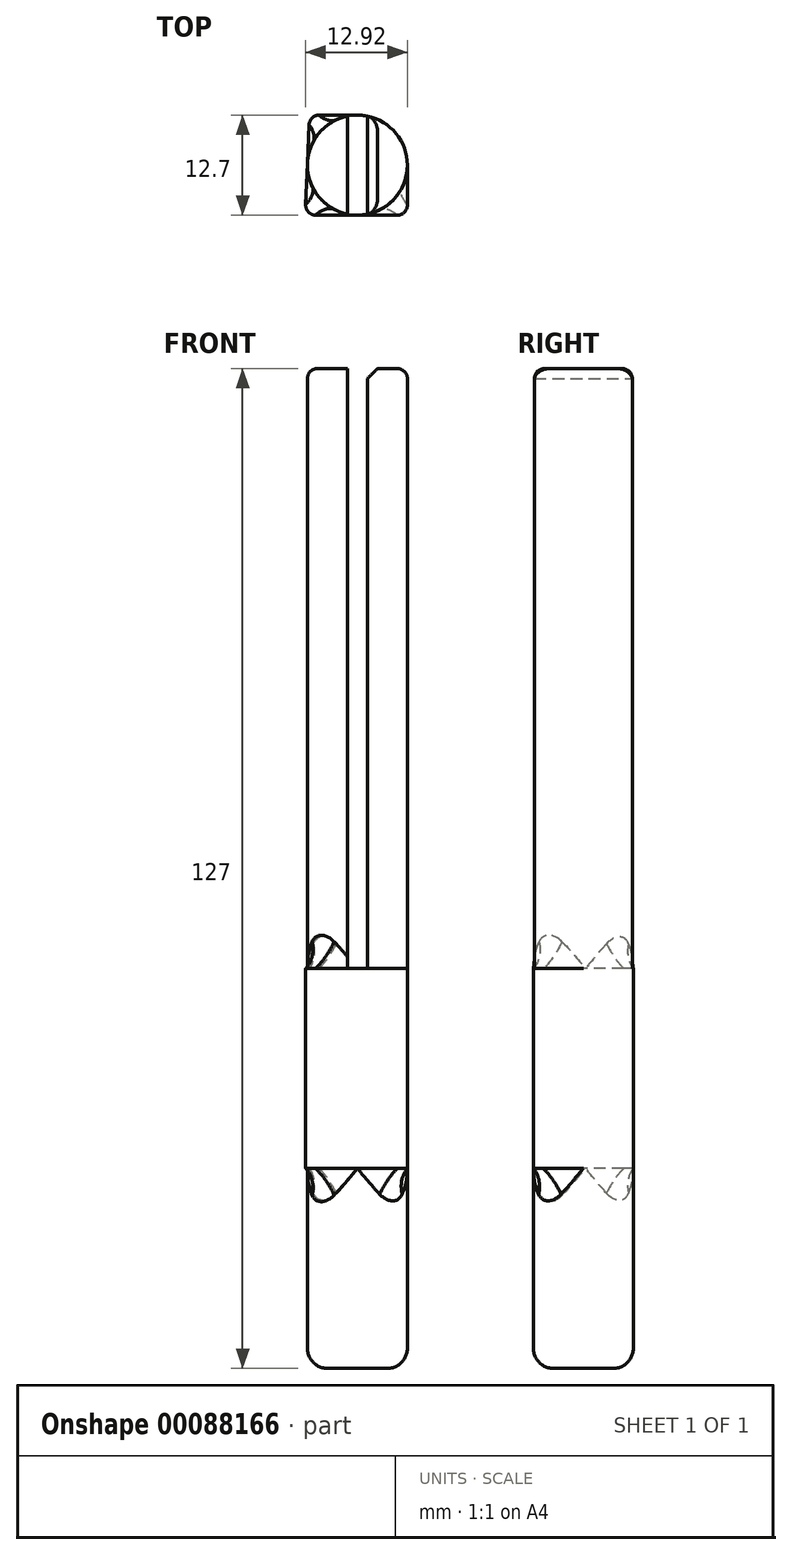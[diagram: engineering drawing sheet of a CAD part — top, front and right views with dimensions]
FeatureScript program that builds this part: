
annotation { "Feature Type Name" : "Feature", "Feature Type Description" : "" }
export const myFeature = defineFeature(function(context is Context, id is Id, definition is map)
    precondition{}
    {
        {
            var Q0;
            Q0=qCreatedBy(makeId("Top.planeOp"),FACE);
            var sketch = newSketch(context, id + "F0", { "sketchPlane" : qUnion([Q0])});
            skCircle(sketch, "E0", {"center": v(0, 0) * mm, "radius": 6.35 * mm});
            skSolve(sketch);
        }
        {
            var Q0;
            Q0=makeQuery(id+"F0.imprint","IMPRINT",FACE,{"disambiguationData":[TD([[makeQuery(id+"F0.imprint","IMPRINT",EDGE,{"derivedFrom":sQuery(id+"F0.wireOp",EDGE,"E0")}),1.0]])]});
            extrude(context, id + "F1", {"entities" : qUnion([Q0]), "depth" : 25.4 * mm});
        }
        {
            var Q0;
            Q0=makeQuery(id+"F1.opExtrude","CAP_FACE",FACE,{"disambiguationData":[OSD([sQuery(id+"F0.wireOp",EDGE,"E0")])],"isStart":false});
            var sketch = newSketch(context, id + "F2", { "sketchPlane" : qUnion([Q0])});
            skLineSegment(sketch, "E1.left", {"start": v(6.35, -6.35) * mm, "end": v(6.35, 6.35) * mm});
            skPoint(sketch, "E1.middle", {"position": v(0, 0) * mm});
            skCircle(sketch, "E2.cCircle", {"center": v(0, 0) * mm, "radius": 6.35 * mm, "construction": true});
            skLineSegment(sketch, "E2.0", {"start": v(6.35, 6.35) * mm, "end": v(6.35, -6.35) * mm});
            skLineSegment(sketch, "E2.1", {"start": v(6.35, -6.35) * mm, "end": v(-6.63, -6.35) * mm});
            skLineSegment(sketch, "E2.2", {"start": v(-6.08, 6.35) * mm, "end": v(6.35, 6.35) * mm});
            skPoint(sketch, "E2.0.midPoint", {"position": v(6.35, 0) * mm});
            skLineSegment(sketch, "E3", {"start": v(-6.08, 6.35) * mm, "end": v(-6.63, -6.35) * mm});
            skSolve(sketch);
        }
        {
            var Q0;
            {var subQ0=sQuery(id+"F2.wireOp",EDGE,"E2.2");var subQ1=sQuery(id+"F2.wireOp",EDGE,"E2.1");var subQ2=makeQuery(id+"F2.imprint","INTERSECT",VERTEX,{"derivedFrom":[subQ1,subQ0]});Q0=makeQuery(id+"F2.imprint","IMPRINT",FACE,{"disambiguationData":[TD([[makeQuery(id+"F2.imprint","IMPRINT",EDGE,{"disambiguationData":[TD([[subQ2,1.0]])],"derivedFrom":subQ1}),-1.0]])]});}
            var Q1;
            {var subQ0=makeQuery(id+"F1.opExtrude","CAP_EDGE",EDGE,{"disambiguationData":[OSD([sQuery(id+"F0.wireOp",EDGE,"E0")])],"isStart":false});var subQ1=makeQuery(id+"F2.imprint","INTERSECT",VERTEX,{"derivedFrom":[subQ0,sQuery(id+"F2.wireOp",EDGE,"E2.0")]});Q1=makeQuery(id+"F2.imprint","IMPRINT",FACE,{"disambiguationData":[TD([[makeQuery(id+"F2.imprint","IMPRINT",EDGE,{"disambiguationData":[TD([[subQ1,1.0]])],"derivedFrom":subQ0}),1.0]])]});}
            var Q2;
            {var subQ0=sQuery(id+"F2.wireOp",EDGE,"E2.2");var subQ1=sQuery(id+"F2.wireOp",EDGE,"E2.0");var subQ2=makeQuery(id+"F2.imprint","INTERSECT",VERTEX,{"derivedFrom":[subQ1,subQ0]});Q2=makeQuery(id+"F2.imprint","IMPRINT",FACE,{"disambiguationData":[TD([[makeQuery(id+"F2.imprint","IMPRINT",EDGE,{"disambiguationData":[TD([[subQ2,-1.0]])],"derivedFrom":subQ1}),-1.0]])]});}
            var Q3;
            {var subQ0=sQuery(id+"F2.wireOp",EDGE,"E2.1");var subQ1=sQuery(id+"F2.wireOp",EDGE,"E2.0");var subQ2=makeQuery(id+"F2.imprint","INTERSECT",VERTEX,{"derivedFrom":[subQ1,subQ0]});Q3=makeQuery(id+"F2.imprint","IMPRINT",FACE,{"disambiguationData":[TD([[makeQuery(id+"F2.imprint","IMPRINT",EDGE,{"disambiguationData":[TD([[subQ2,1.0]])],"derivedFrom":subQ1}),-1.0]])]});}
            var Q4;
            {var subQ0=sQuery(id+"F2.wireOp",EDGE,"E3");var subQ1=sQuery(id+"F2.wireOp",EDGE,"E2.2");var subQ2=makeQuery(id+"F2.imprint","INTERSECT",VERTEX,{"derivedFrom":[subQ1,subQ0]});Q4=makeQuery(id+"F2.imprint","IMPRINT",FACE,{"disambiguationData":[TD([[makeQuery(id+"F2.imprint","IMPRINT",EDGE,{"disambiguationData":[TD([[subQ2,-1.0]])],"derivedFrom":subQ1}),-1.0]])]});}
            extrude(context, id + "F3", {"entities" : qUnion([Q0, Q1, Q2, Q3, Q4]), "operationType" : NewBodyOperationType.ADD, "depth" : 25.4 * mm, "offsetDistance" : 25.4 * mm});
        }
        {
            var Q0;
            Q0=makeQuery(id+"F3.opExtrude","CAP_FACE",FACE,{"disambiguationData":[OSD([sQuery(id+"F2.wireOp",EDGE,"E2.0"),sQuery(id+"F2.wireOp",EDGE,"E2.1"),sQuery(id+"F2.wireOp",EDGE,"E2.2")])],"isStart":false});
            var sketch = newSketch(context, id + "F4", { "sketchPlane" : qUnion([Q0])});
            skCircle(sketch, "E4", {"center": v(0, 0) * mm, "radius": 6.35 * mm});
            skSolve(sketch);
        }
        {
            var Q0;
            {var subQ0=sQuery(id+"F4.wireOp",EDGE,"E4");var subQ1=makeQuery(id+"F4.imprint","INTERSECT",VERTEX,{"derivedFrom":[makeQuery(id+"F3.opExtrude","CAP_EDGE",EDGE,{"disambiguationData":[OSD([sQuery(id+"F2.wireOp",EDGE,"E1.top")])],"isStart":false}),subQ0]});Q0=makeQuery(id+"F4.imprint","IMPRINT",FACE,{"disambiguationData":[TD([[makeQuery(id+"F4.imprint","IMPRINT",EDGE,{"disambiguationData":[TD([[subQ1,1.0]])],"derivedFrom":subQ0}),1.0]])]});}
            extrude(context, id + "F5", {"entities" : qUnion([Q0]), "operationType" : NewBodyOperationType.ADD, "depth" : 76.2 * mm});
        }
        {
            var Q0;
            Q0=makeQuery(id+"F5.opExtrude","CAP_FACE",FACE,{"disambiguationData":[OSD([sQuery(id+"F4.wireOp",EDGE,"E4")])],"isStart":false});
            var sketch = newSketch(context, id + "F6", { "sketchPlane" : qUnion([Q0])});
            skLineSegment(sketch, "E5.bottom", {"start": v(1.27, 6.35) * mm, "end": v(-1.27, 6.35) * mm});
            skLineSegment(sketch, "E5.top", {"start": v(1.27, -6.35) * mm, "end": v(-1.27, -6.35) * mm});
            skLineSegment(sketch, "E5.left", {"start": v(1.27, 6.35) * mm, "end": v(1.27, -6.35) * mm});
            skLineSegment(sketch, "E5.right", {"start": v(-1.27, 6.35) * mm, "end": v(-1.27, -6.35) * mm});
            skPoint(sketch, "E5.middle", {"position": v(0, 0) * mm});
            skSolve(sketch);
        }
        {
            var Q0;
            {var subQ0=makeQuery(id+"F5.opExtrude","CAP_EDGE",EDGE,{"disambiguationData":[OSD([sQuery(id+"F4.wireOp",EDGE,"E4")])],"isStart":false});var subQ5=sQuery(id+"F6.wireOp",EDGE,"E5.left");var subQ6=makeQuery(id+"F6.imprint","INTERSECT",VERTEX,{"disambiguationData":[OD(0.0)],"derivedFrom":[subQ0,subQ5]});Q0=makeQuery(id+"F6.imprint","IMPRINT",FACE,{"disambiguationData":[TD([[makeQuery(id+"F6.imprint","IMPRINT",EDGE,{"disambiguationData":[TD([[subQ6,-1.0]])],"derivedFrom":subQ5}),-1.0]])]});}
            extrude(context, id + "F7", {"entities" : qUnion([Q0]), "operationType" : NewBodyOperationType.REMOVE, "oppositeDirection" : true, "depth" : 76.2 * mm});
        }
        {
            var Q0;
            Q0=makeQuery(id+"F7.boolean.opBoolean","COPY",EDGE,{"derivedFrom":makeQuery(id+"F7.opExtrude","CAP_EDGE",EDGE,{"disambiguationData":[OSD([sQuery(id+"F6.wireOp",EDGE,"E5.right")])],"isStart":true})});
            var Q1;
            Q1=makeQuery(id+"F7.boolean.opBoolean","COPY",EDGE,{"derivedFrom":makeQuery(id+"F7.opExtrude","CAP_EDGE",EDGE,{"disambiguationData":[OSD([sQuery(id+"F6.wireOp",EDGE,"E5.left")])],"isStart":true})});
            chamfer(context, id + "F8", {"entities" : qUnion([Q0, Q1]), "width" : 1.27 * mm, "tangentPropagation" : true});
        }
        {
            var Q0;
            {var subQ0=sQuery(id+"F4.wireOp",EDGE,"E4");Q0=makeQuery(id+"F7.boolean.opBoolean","SPLIT",EDGE,{"disambiguationData":[TD([makeQuery(id+"F7.opExtrude","SWEPT_FACE",FACE,{"disambiguationData":[OSD([sQuery(id+"F6.wireOp",EDGE,"E5.left")])]})])],"derivedFrom":makeQuery(id+"F5.opExtrude","CAP_EDGE",EDGE,{"disambiguationData":[OSD([subQ0])],"isStart":false})});}
            var Q1;
            {var subQ0=sQuery(id+"F4.wireOp",EDGE,"E4");Q1=makeQuery(id+"F7.boolean.opBoolean","SPLIT",EDGE,{"disambiguationData":[TD([makeQuery(id+"F7.opExtrude","SWEPT_FACE",FACE,{"disambiguationData":[OSD([sQuery(id+"F6.wireOp",EDGE,"E5.right")])]})])],"derivedFrom":makeQuery(id+"F5.opExtrude","CAP_EDGE",EDGE,{"disambiguationData":[OSD([subQ0])],"isStart":false})});}
            fillet(context, id + "F9", {"entities" : qUnion([Q0, Q1]), "radius" : 1.27 * mm, "tangentPropagation" : true, "allowEdgeOverflow" : false});
        }
        {
            var Q0;
            Q0=makeQuery(id+"F3.opExtrude","SWEPT_EDGE",EDGE,{"disambiguationData":[OSD([sQuery(id+"F2.wireOp",EDGE,"E2.0"),sQuery(id+"F2.wireOp",EDGE,"E2.2")])]});
            var Q1;
            Q1=makeQuery(id+"F3.opExtrude","SWEPT_EDGE",EDGE,{"disambiguationData":[OSD([sQuery(id+"F2.wireOp",EDGE,"E2.0"),sQuery(id+"F2.wireOp",EDGE,"E2.1")])]});
            var Q2;
            Q2=makeQuery(id+"F3.opExtrude","SWEPT_EDGE",EDGE,{"disambiguationData":[OSD([sQuery(id+"F2.wireOp",EDGE,"E2.1"),sQuery(id+"F2.wireOp",EDGE,"E2.2")])]});
            fillet(context, id + "F10", {"entities" : qUnion([Q0, Q1, Q2]), "radius" : 1.27 * mm, "tangentPropagation" : true, "allowEdgeOverflow" : false});
        }
        {
            var Q0;
            {var subQ1=sQuery(id+"F4.wireOp",EDGE,"E4");var subQ2=makeQuery(id+"F5.opExtrude","SWEPT_FACE",FACE,{"disambiguationData":[OSD([subQ1])]});var subQ3=sQuery(id+"F2.wireOp",EDGE,"E2.2");var subQ4=sQuery(id+"F2.wireOp",EDGE,"E2.0");var subQ5=makeQuery(id+"F3.opExtrude","CAP_FACE",FACE,{"disambiguationData":[OSD([subQ4,sQuery(id+"F2.wireOp",EDGE,"E2.1"),subQ3])],"isStart":false});var subQ6=makeQuery(id+"F3.opExtrude","SWEPT_FACE",FACE,{"disambiguationData":[OSD([subQ4])]});Q0=makeQuery(id+"F7.boolean.opBoolean","SPLIT",EDGE,{"disambiguationData":[TD([subQ6])],"derivedFrom":makeQuery(id+"F5.boolean.opBoolean","SPLIT",EDGE,{"disambiguationData":[TD([subQ6,subQ5,makeQuery(id+"F3.opExtrude","SWEPT_FACE",FACE,{"disambiguationData":[OSD([subQ3])]}),subQ2])],"derivedFrom":makeQuery(id+"F5.opExtrude","CAP_EDGE",EDGE,{"disambiguationData":[OSD([subQ1])],"isStart":true})})});}
            var Q1;
            {var subQ1=sQuery(id+"F4.wireOp",EDGE,"E4");var subQ2=makeQuery(id+"F5.opExtrude","SWEPT_FACE",FACE,{"disambiguationData":[OSD([subQ1])]});var subQ3=sQuery(id+"F2.wireOp",EDGE,"E2.1");var subQ4=sQuery(id+"F2.wireOp",EDGE,"E2.0");var subQ5=makeQuery(id+"F3.opExtrude","CAP_FACE",FACE,{"disambiguationData":[OSD([subQ4,subQ3,sQuery(id+"F2.wireOp",EDGE,"E2.2")])],"isStart":false});var subQ6=makeQuery(id+"F3.opExtrude","SWEPT_FACE",FACE,{"disambiguationData":[OSD([subQ4])]});Q1=makeQuery(id+"F7.boolean.opBoolean","SPLIT",EDGE,{"disambiguationData":[TD([subQ6])],"derivedFrom":makeQuery(id+"F5.boolean.opBoolean","SPLIT",EDGE,{"disambiguationData":[TD([subQ6,subQ5,makeQuery(id+"F3.opExtrude","SWEPT_FACE",FACE,{"disambiguationData":[OSD([subQ3])]}),subQ2])],"derivedFrom":makeQuery(id+"F5.opExtrude","CAP_EDGE",EDGE,{"disambiguationData":[OSD([subQ1])],"isStart":true})})});}
            var Q2;
            {var subQ0=sQuery(id+"F2.wireOp",EDGE,"E2.2");var subQ1=sQuery(id+"F2.wireOp",EDGE,"E2.1");var subQ2=sQuery(id+"F4.wireOp",EDGE,"E4");Q2=makeQuery(id+"F5.boolean.opBoolean","SPLIT",EDGE,{"disambiguationData":[TD([makeQuery(id+"F3.opExtrude","CAP_FACE",FACE,{"disambiguationData":[OSD([sQuery(id+"F2.wireOp",EDGE,"E2.0"),subQ1,subQ0])],"isStart":false}),makeQuery(id+"F3.opExtrude","SWEPT_FACE",FACE,{"disambiguationData":[OSD([subQ1])]}),makeQuery(id+"F3.opExtrude","SWEPT_FACE",FACE,{"disambiguationData":[OSD([subQ0])]}),makeQuery(id+"F5.opExtrude","SWEPT_FACE",FACE,{"disambiguationData":[OSD([subQ2])]})])],"derivedFrom":makeQuery(id+"F5.opExtrude","CAP_EDGE",EDGE,{"disambiguationData":[OSD([subQ2])],"isStart":true})});}
            var Q3;
            {var subQ0=sQuery(id+"F0.wireOp",EDGE,"E0");var subQ1=sQuery(id+"F2.wireOp",EDGE,"E2.2");var subQ2=sQuery(id+"F2.wireOp",EDGE,"E2.1");Q3=makeQuery(id+"F3.boolean.opBoolean","SPLIT",EDGE,{"disambiguationData":[TD([makeQuery(id+"F1.opExtrude","SWEPT_FACE",FACE,{"disambiguationData":[OSD([subQ0])]}),makeQuery(id+"F3.opExtrude","CAP_FACE",FACE,{"disambiguationData":[OSD([sQuery(id+"F2.wireOp",EDGE,"E2.0"),subQ2,subQ1])],"isStart":true}),makeQuery(id+"F3.opExtrude","SWEPT_FACE",FACE,{"disambiguationData":[OSD([subQ2])]}),makeQuery(id+"F3.opExtrude","SWEPT_FACE",FACE,{"disambiguationData":[OSD([subQ1])]})])],"derivedFrom":makeQuery(id+"F1.opExtrude","CAP_EDGE",EDGE,{"disambiguationData":[OSD([subQ0])],"isStart":false})});}
            var Q4;
            {var subQ0=sQuery(id+"F0.wireOp",EDGE,"E0");var subQ1=sQuery(id+"F2.wireOp",EDGE,"E2.0");var subQ2=sQuery(id+"F2.wireOp",EDGE,"E2.2");Q4=makeQuery(id+"F3.boolean.opBoolean","SPLIT",EDGE,{"disambiguationData":[TD([makeQuery(id+"F1.opExtrude","SWEPT_FACE",FACE,{"disambiguationData":[OSD([subQ0])]}),makeQuery(id+"F3.opExtrude","SWEPT_FACE",FACE,{"disambiguationData":[OSD([subQ1])]}),makeQuery(id+"F3.opExtrude","CAP_FACE",FACE,{"disambiguationData":[OSD([subQ1,sQuery(id+"F2.wireOp",EDGE,"E2.1"),subQ2])],"isStart":true}),makeQuery(id+"F3.opExtrude","SWEPT_FACE",FACE,{"disambiguationData":[OSD([subQ2])]})])],"derivedFrom":makeQuery(id+"F1.opExtrude","CAP_EDGE",EDGE,{"disambiguationData":[OSD([subQ0])],"isStart":false})});}
            var Q5;
            {var subQ0=sQuery(id+"F0.wireOp",EDGE,"E0");var subQ1=sQuery(id+"F2.wireOp",EDGE,"E2.0");var subQ2=sQuery(id+"F2.wireOp",EDGE,"E2.1");Q5=makeQuery(id+"F3.boolean.opBoolean","SPLIT",EDGE,{"disambiguationData":[TD([makeQuery(id+"F1.opExtrude","SWEPT_FACE",FACE,{"disambiguationData":[OSD([subQ0])]}),makeQuery(id+"F3.opExtrude","SWEPT_FACE",FACE,{"disambiguationData":[OSD([subQ1])]}),makeQuery(id+"F3.opExtrude","CAP_FACE",FACE,{"disambiguationData":[OSD([subQ1,subQ2,sQuery(id+"F2.wireOp",EDGE,"E2.2")])],"isStart":true}),makeQuery(id+"F3.opExtrude","SWEPT_FACE",FACE,{"disambiguationData":[OSD([subQ2])]})])],"derivedFrom":makeQuery(id+"F1.opExtrude","CAP_EDGE",EDGE,{"disambiguationData":[OSD([subQ0])],"isStart":false})});}
            fillet(context, id + "F11", {"entities" : qUnion([Q0, Q1, Q2, Q3, Q4, Q5]), "radius" : 5.08 * mm, "tangentPropagation" : true, "allowEdgeOverflow" : false});
        }
        {
            var Q0;
            Q0=makeQuery(id+"F1.opExtrude","CAP_EDGE",EDGE,{"disambiguationData":[OSD([sQuery(id+"F0.wireOp",EDGE,"E0")])],"isStart":true});
            fillet(context, id + "F12", {"entities" : qUnion([Q0]), "radius" : 2.54 * mm, "tangentPropagation" : true, "allowEdgeOverflow" : false});
        }
    });
